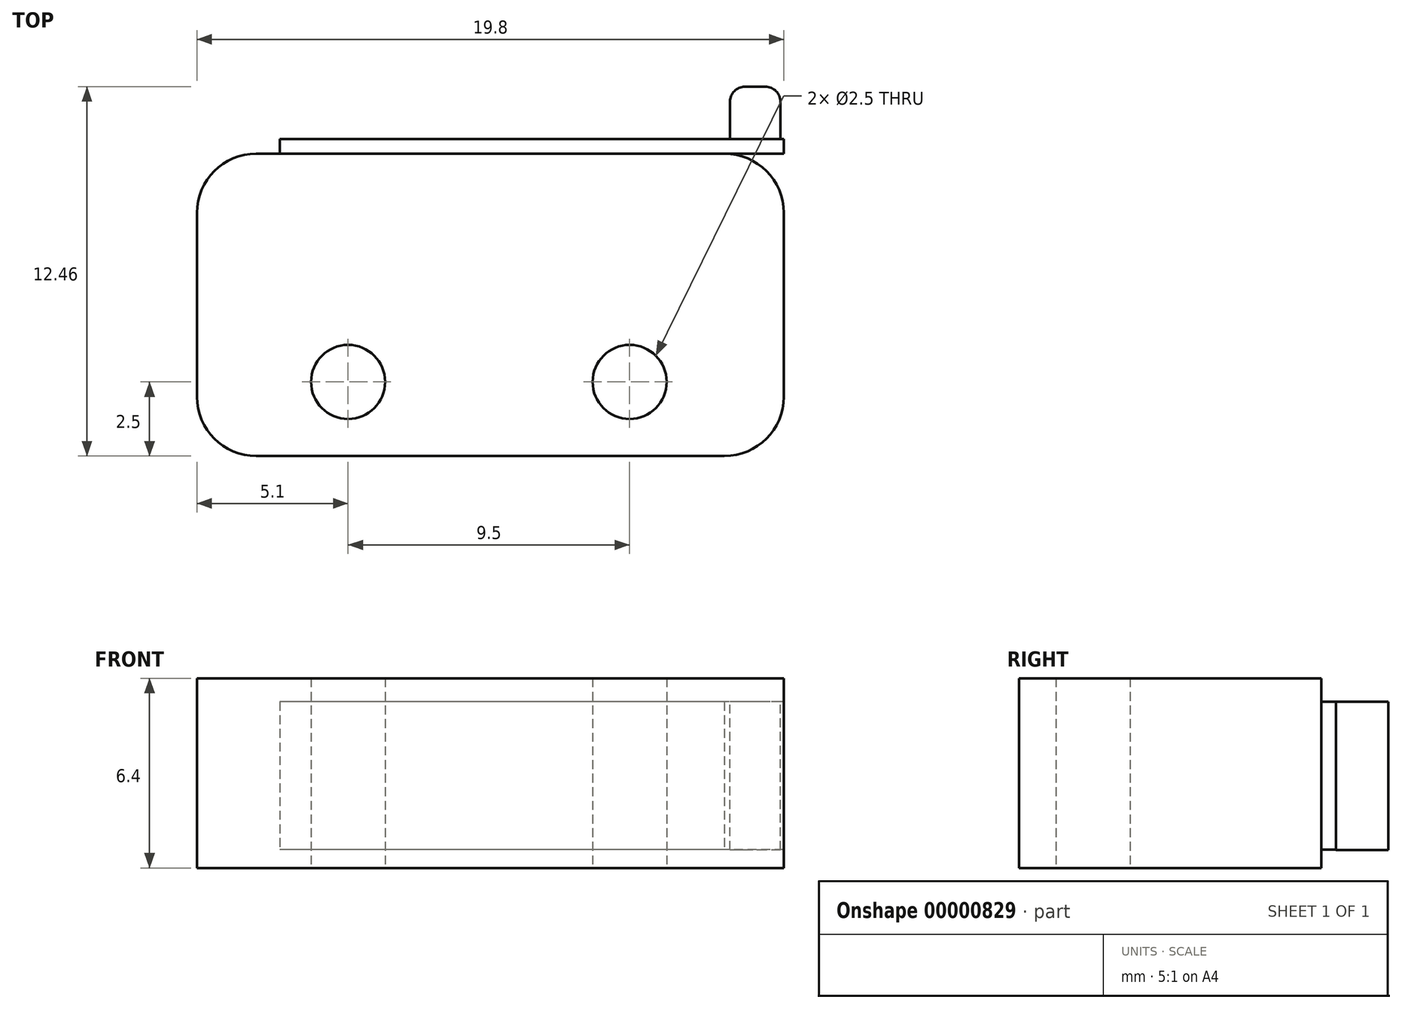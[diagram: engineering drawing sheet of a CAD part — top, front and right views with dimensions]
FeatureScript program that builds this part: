
annotation { "Feature Type Name" : "Feature", "Feature Type Description" : "" }
export const myFeature = defineFeature(function(context is Context, id is Id, definition is map)
    precondition{}
    {
        {
            var Q0;
            Q0=qCreatedBy(makeId("Top.planeOp"),FACE);
            var sketch = newSketch(context, id + "F0", { "sketchPlane" : qUnion([Q0])});
            skLineSegment(sketch, "E0.rect.bottom", {"start": v(9.9, -5.1) * mm, "end": v(-9.9, -5.1) * mm});
            skLineSegment(sketch, "E0.rect.top", {"start": v(9.9, 5.1) * mm, "end": v(-9.9, 5.1) * mm});
            skLineSegment(sketch, "E0.rect.left", {"start": v(9.9, -5.1) * mm, "end": v(9.9, 5.1) * mm});
            skLineSegment(sketch, "E0.rect.right", {"start": v(-9.9, -5.1) * mm, "end": v(-9.9, 5.1) * mm});
            skPoint(sketch, "E0.rect.middle", {"position": v(0, 0) * mm});
            skLineSegment(sketch, "E1", {"start": v(-11.22, -2.6) * mm, "end": v(12.45, -2.6) * mm, "construction": true});
            skCircle(sketch, "E2", {"center": v(-4.8, -2.6) * mm, "radius": 1.25 * mm});
            skCircle(sketch, "E3", {"center": v(4.7, -2.6) * mm, "radius": 1.25 * mm});
            skSolve(sketch);
        }
        {
            var Q0;
            Q0=makeQuery(id+"F0.imprint","IMPRINT",FACE,{"disambiguationData":[TD([[makeQuery(id+"F0.imprint","IMPRINT",EDGE,{"derivedFrom":sQuery(id+"F0.wireOp",EDGE,"E0.rect.bottom")}),-1.0]])]});
            extrude(context, id + "F1", {"entities" : qUnion([Q0]), "depth" : 6.4 * mm});
        }
        {
            var Q0;
            Q0=makeQuery(id+"F1.opExtrude","SWEPT_EDGE",EDGE,{"disambiguationData":[OSD([sQuery(id+"F0.wireOp",EDGE,"E0.rect.top"),sQuery(id+"F0.wireOp",EDGE,"E0.rect.left")])]});
            var Q1;
            Q1=makeQuery(id+"F1.opExtrude","SWEPT_EDGE",EDGE,{"disambiguationData":[OSD([sQuery(id+"F0.wireOp",EDGE,"E0.rect.top"),sQuery(id+"F0.wireOp",EDGE,"E0.rect.right")])]});
            var Q2;
            Q2=makeQuery(id+"F1.opExtrude","SWEPT_EDGE",EDGE,{"disambiguationData":[OSD([sQuery(id+"F0.wireOp",EDGE,"E0.rect.bottom"),sQuery(id+"F0.wireOp",EDGE,"E0.rect.left")])]});
            var Q3;
            Q3=makeQuery(id+"F1.opExtrude","SWEPT_EDGE",EDGE,{"disambiguationData":[OSD([sQuery(id+"F0.wireOp",EDGE,"E0.rect.bottom"),sQuery(id+"F0.wireOp",EDGE,"E0.rect.right")])]});
            fillet(context, id + "F2", {"entities" : qUnion([Q0, Q1, Q2, Q3]), "radius" : 2 * mm, "tangentPropagation" : true, "allowEdgeOverflow" : false});
        }
        {
            var Q0;
            Q0=makeQuery(id+"F1.opExtrude","SWEPT_FACE",FACE,{"disambiguationData":[OSD([sQuery(id+"F0.wireOp",EDGE,"E0.rect.top")])]});
            var sketch = newSketch(context, id + "F3", { "sketchPlane" : qUnion([Q0])});
            skLineSegment(sketch, "E4.rect.bottom", {"start": v(-9.9, 5.6) * mm, "end": v(7.1, 5.6) * mm});
            skLineSegment(sketch, "E4.rect.top", {"start": v(-9.9, 0.62) * mm, "end": v(7.1, 0.62) * mm});
            skLineSegment(sketch, "E4.rect.left", {"start": v(-9.9, 5.6) * mm, "end": v(-9.9, 0.62) * mm});
            skLineSegment(sketch, "E4.rect.right", {"start": v(7.1, 5.6) * mm, "end": v(7.1, 0.62) * mm});
            skPoint(sketch, "E4.rect.middle", {"position": v(-1.4, 3.11) * mm});
            skSolve(sketch);
        }
        {
            var Q0;
            {var subQ7=sQuery(id+"F3.wireOp",EDGE,"E4.rect.left");var subQ8=sQuery(id+"F3.wireOp",EDGE,"E4.rect.right");Q0=qUnion([makeQuery(id+"F3.imprint","IMPRINT",FACE,{"disambiguationData":[TD([[makeQuery(id+"F3.imprint","IMPRINT",EDGE,{"derivedFrom":subQ7}),1.0]])]}),makeQuery(id+"F3.imprint","IMPRINT",FACE,{"disambiguationData":[TD([[makeQuery(id+"F3.imprint","IMPRINT",EDGE,{"derivedFrom":subQ8}),-1.0]])]})]);}
            extrude(context, id + "F4", {"entities" : qUnion([Q0]), "operationType" : NewBodyOperationType.ADD, "depth" : .5 * mm});
        }
        {
            var Q0;
            Q0=makeQuery(id+"F4.opExtrude","SWEPT_FACE",FACE,{"disambiguationData":[OSD([sQuery(id+"F3.wireOp",EDGE,"E4.rect.bottom")])]});
            var sketch = newSketch(context, id + "F5", { "sketchPlane" : qUnion([Q0])});
            skLineSegment(sketch, "E5.rect.bottom", {"start": v(9.78, 5.6) * mm, "end": v(8.09, 5.6) * mm});
            skLineSegment(sketch, "E5.rect.top", {"start": v(9.28, 7.36) * mm, "end": v(8.59, 7.36) * mm});
            skLineSegment(sketch, "E5.rect.left", {"start": v(9.78, 5.6) * mm, "end": v(9.78, 6.86) * mm});
            skLineSegment(sketch, "E5.rect.right", {"start": v(8.09, 5.6) * mm, "end": v(8.09, 6.86) * mm});
            skPoint(sketch, "E5.rect.middle", {"position": v(8.94, 6.48) * mm});
            skPoint(sketch, "E6.visualSharp", {"position": v(8.09, 7.36) * mm});
            skArc(sketch, "E6.filletArc", {"start": v(8.59, 7.36) * mm, "mid": v(8.23, 7.21) * mm, "end": v(8.09, 6.86) * mm});
            skPoint(sketch, "E7.visualSharp", {"position": v(9.78, 7.36) * mm});
            skArc(sketch, "E7.filletArc", {"start": v(9.78, 6.86) * mm, "mid": v(9.64, 7.21) * mm, "end": v(9.28, 7.36) * mm});
            skSolve(sketch);
        }
        {
            var Q0;
            Q0 = qSketchRegion(id + "F5", true);
            extrude(context, id + "F6", {"entities" : qUnion([Q0]), "oppositeDirection" : true, "depth" : 5 * mm});
        }
    });
